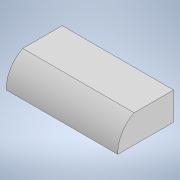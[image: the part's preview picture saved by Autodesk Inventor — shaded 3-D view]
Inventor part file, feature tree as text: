
AUTODESK INVENTOR PART (.ipt)
format: ipt  version: 2020 (Build 240168000, 168)  size: 131,072 bytes
history: native  units: in
note: dims shown in document units (in); Inventor stores cm internally (conversion verified against a paired STEP export)
features: extrude x3, sketch x3
ambient origin geometry x8: Origin, YZ Plane, XZ Plane, XY Plane, X Axis, Y Axis, Z Axis, Center Point
bodies: Solid1 (feature_tree)
feature tree (6):
  extrude  "Extrusion1"  Depth=1.9685in
  extrude  "Extrusion2"  Depth=0.1969in
  extrude  "Extrusion3"  Depth=0.1969in
  sketch  "Sketch1"  dims[d0=3.937in d1=1.9685in]
  sketch  "Sketch4"  dims[d2=7.874in d3=0.0in d5=0.1969in]
  sketch  "Sketch5"  dims[d6=0.1969in d7=0.1969in d8=0.1969in d9=2.7559in d10=0.0in d11=0.1181in d12=0.1181in d13=0.1181in d14=0.1181in d15=0.3937in d16=0.3937in d17=0.3937in d18=0.3937in d19=0.3937in d20=0.3937in d22=0.3937in d23=0.3937in d24=0.3937in d25=0.0in d4=0.0197in d26=0.0197in d27=0.0344in]
